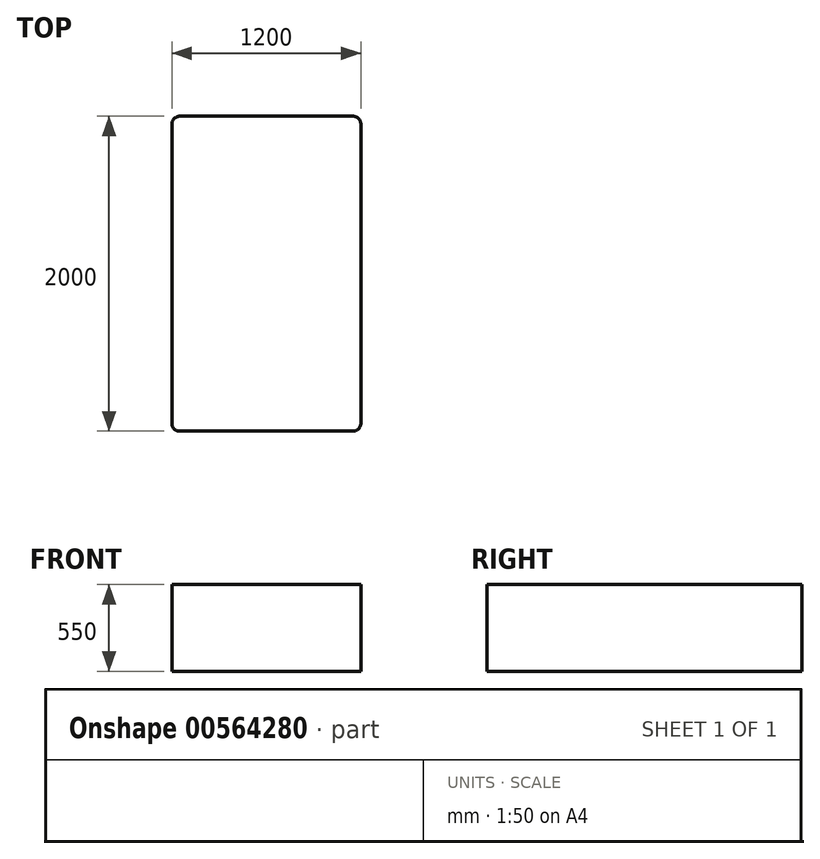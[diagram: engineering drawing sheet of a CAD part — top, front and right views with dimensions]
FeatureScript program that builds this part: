
annotation { "Feature Type Name" : "Feature", "Feature Type Description" : "" }
export const myFeature = defineFeature(function(context is Context, id is Id, definition is map)
    precondition{}
    {
        {
            var Q0;
            Q0=qCreatedBy(makeId("Top.planeOp"),FACE);
            var sketch = newSketch(context, id + "F0", { "sketchPlane" : qUnion([Q0])});
            skLineSegment(sketch, "E0.bottom", {"start": v(-590.6, 1413.66) * mm, "end": v(609.4, 1413.66) * mm});
            skLineSegment(sketch, "E0.top", {"start": v(-590.6, -586.34) * mm, "end": v(609.4, -586.34) * mm});
            skLineSegment(sketch, "E0.left", {"start": v(-590.6, 1413.66) * mm, "end": v(-590.6, -586.34) * mm});
            skLineSegment(sketch, "E0.right", {"start": v(609.4, 1413.66) * mm, "end": v(609.4, -586.34) * mm});
            skSolve(sketch);
        }
        {
            var Q0;
            Q0=makeQuery(id+"F0.imprint","IMPRINT",FACE,{"disambiguationData":[TD([[makeQuery(id+"F0.imprint","IMPRINT",EDGE,{"derivedFrom":sQuery(id+"F0.wireOp",EDGE,"E0.bottom")}),-1.0]])]});
            extrude(context, id + "F1", {"entities" : qUnion([Q0]), "depth" : 550 * mm, "offsetDistance" : 25 * mm});
        }
        {
            var Q0;
            Q0=makeQuery(id+"F1.opExtrude","SWEPT_EDGE",EDGE,{"disambiguationData":[OSD([sQuery(id+"F0.wireOp",EDGE,"E0.top"),sQuery(id+"F0.wireOp",EDGE,"E0.right")])]});
            fillet(context, id + "F2", {"entities" : qUnion([Q0]), "radius" : 50 * mm, "tangentPropagation" : true, "allowEdgeOverflow" : false});
        }
        {
            var Q0;
            Q0=makeQuery(id+"F1.opExtrude","SWEPT_EDGE",EDGE,{"disambiguationData":[OSD([sQuery(id+"F0.wireOp",EDGE,"E0.top"),sQuery(id+"F0.wireOp",EDGE,"E0.left")])]});
            fillet(context, id + "F3", {"entities" : qUnion([Q0]), "radius" : 50 * mm, "tangentPropagation" : true, "allowEdgeOverflow" : false});
        }
        {
            var Q0;
            Q0=makeQuery(id+"F1.opExtrude","SWEPT_EDGE",EDGE,{"disambiguationData":[OSD([sQuery(id+"F0.wireOp",EDGE,"E0.bottom"),sQuery(id+"F0.wireOp",EDGE,"E0.right")])]});
            var Q1;
            Q1=makeQuery(id+"F1.opExtrude","SWEPT_EDGE",EDGE,{"disambiguationData":[OSD([sQuery(id+"F0.wireOp",EDGE,"E0.bottom"),sQuery(id+"F0.wireOp",EDGE,"E0.left")])]});
            fillet(context, id + "F4", {"entities" : qUnion([Q0, Q1]), "radius" : 50 * mm, "tangentPropagation" : true, "allowEdgeOverflow" : false});
        }
    });
